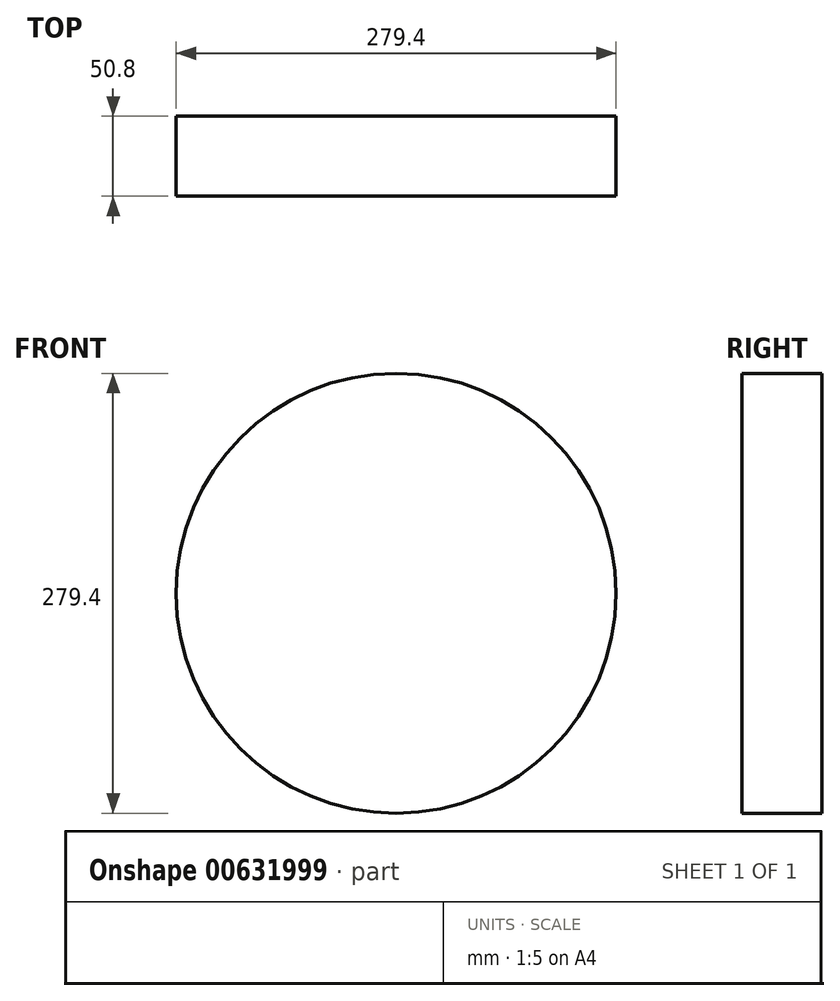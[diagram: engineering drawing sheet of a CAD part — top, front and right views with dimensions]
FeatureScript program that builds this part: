
annotation { "Feature Type Name" : "Feature", "Feature Type Description" : "" }
export const myFeature = defineFeature(function(context is Context, id is Id, definition is map)
    precondition{}
    {
        {
            var Q0;
            Q0=qCreatedBy(makeId("Front.planeOp"),FACE);
            var sketch = newSketch(context, id + "F0", { "sketchPlane" : qUnion([Q0])});
            skCircle(sketch, "E0", {"center": v(0, 0) * mm, "radius": 139.7 * mm});
            skSolve(sketch);
        }
        {
            var Q0;
            Q0=makeQuery(id+"F0.imprint","IMPRINT",FACE,{"disambiguationData":[TD([[makeQuery(id+"F0.imprint","IMPRINT",EDGE,{"derivedFrom":sQuery(id+"F0.wireOp",EDGE,"E0")}),1.0]])]});
            extrude(context, id + "F1", {"entities" : qUnion([Q0]), "depth" : 50.8 * mm, "offsetDistance" : 25.4 * mm});
        }
    });
